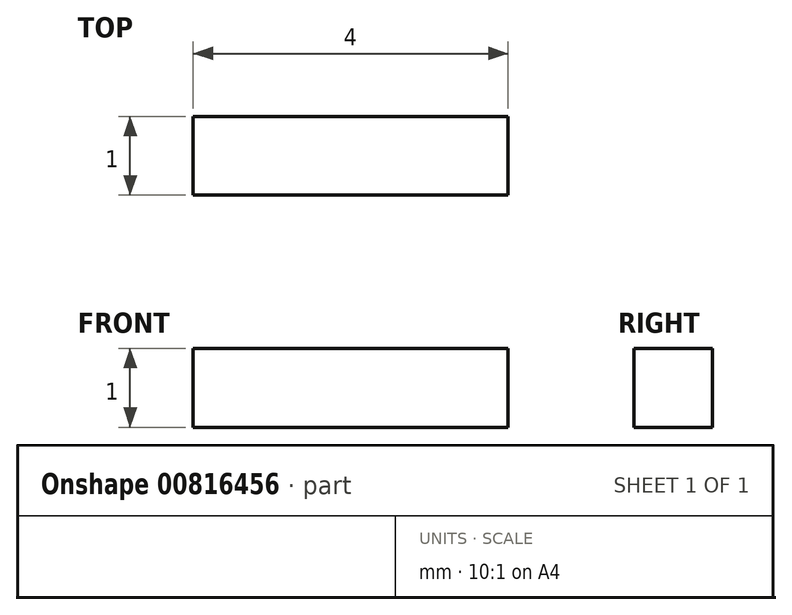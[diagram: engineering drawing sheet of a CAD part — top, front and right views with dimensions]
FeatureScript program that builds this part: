
annotation { "Feature Type Name" : "Feature", "Feature Type Description" : "" }
export const myFeature = defineFeature(function(context is Context, id is Id, definition is map)
    precondition{}
    {
        {
            var Q0;
            Q0=qCreatedBy(makeId("Top.planeOp"),FACE);
            var sketch = newSketch(context, id + "F0", { "sketchPlane" : qUnion([Q0])});
            skLineSegment(sketch, "E0.bottom", {"start": v(-19.54, 1.17) * mm, "end": v(-15.54, 1.17) * mm});
            skLineSegment(sketch, "E0.top", {"start": v(-19.54, 0.17) * mm, "end": v(-15.54, 0.17) * mm});
            skLineSegment(sketch, "E0.left", {"start": v(-19.54, 1.17) * mm, "end": v(-19.54, 0.17) * mm});
            skLineSegment(sketch, "E0.right", {"start": v(-15.54, 1.17) * mm, "end": v(-15.54, 0.17) * mm});
            skSolve(sketch);
        }
        {
            var Q0;
            Q0=makeQuery(id+"F0.imprint","IMPRINT",FACE,{"disambiguationData":[TD([[makeQuery(id+"F0.imprint","IMPRINT",EDGE,{"derivedFrom":sQuery(id+"F0.wireOp",EDGE,"E0.bottom")}),-1.0]])]});
            extrude(context, id + "F1", {"entities" : qUnion([Q0]), "depth" : 1 * mm, "offsetDistance" : 25 * mm});
        }
    });
